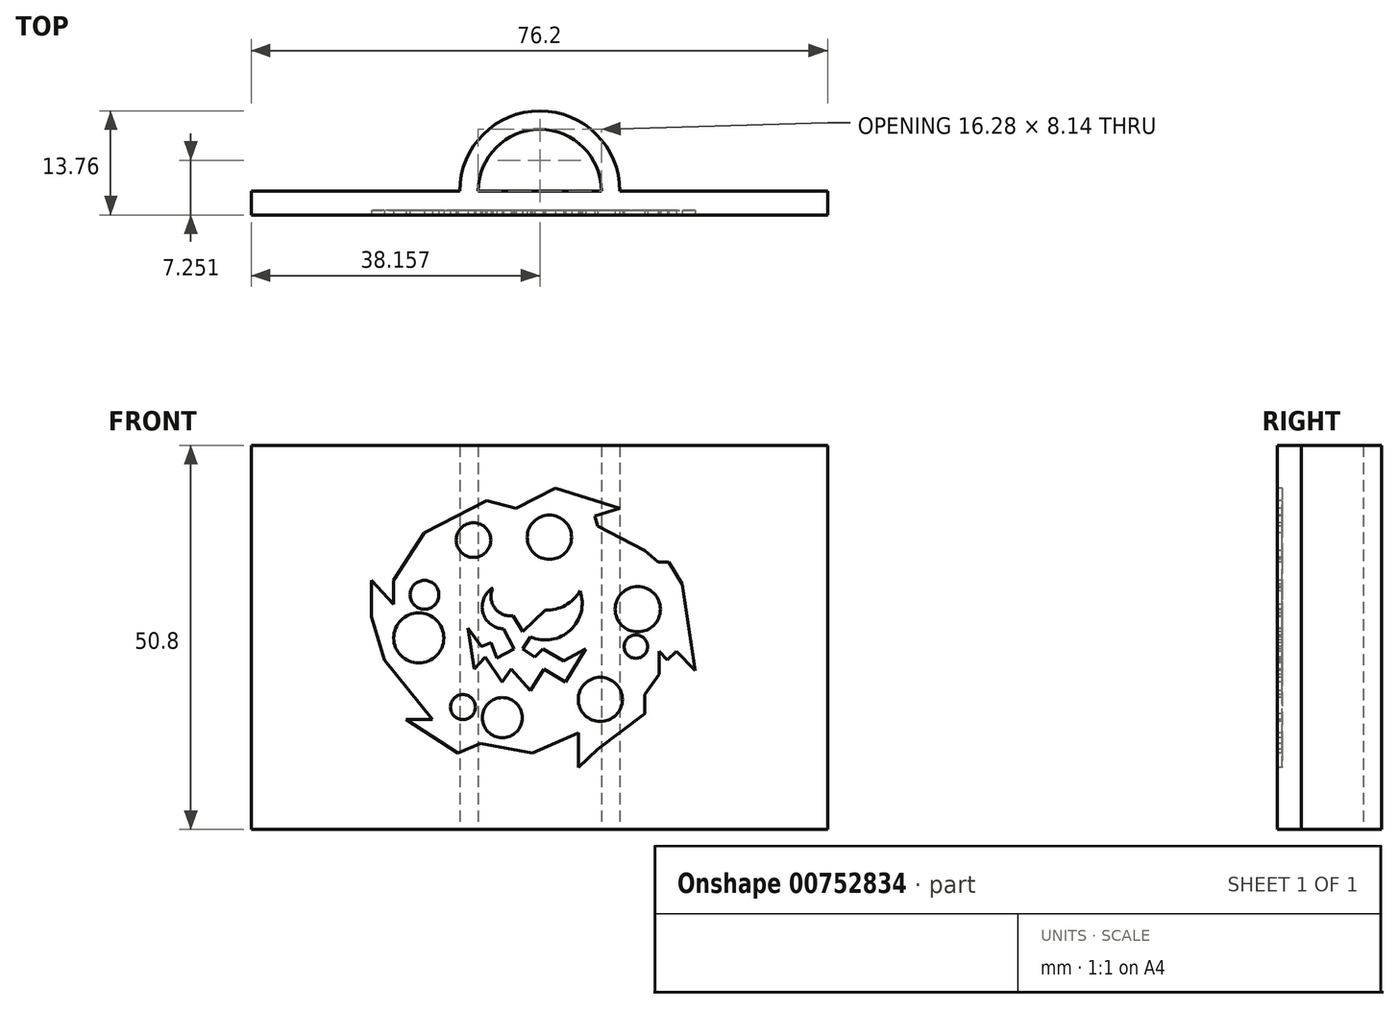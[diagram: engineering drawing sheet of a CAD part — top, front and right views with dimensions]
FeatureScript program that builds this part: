
annotation { "Feature Type Name" : "Feature", "Feature Type Description" : "" }
export const myFeature = defineFeature(function(context is Context, id is Id, definition is map)
    precondition{}
    {
        {
            var Q0;
            Q0=qCreatedBy(makeId("Front.planeOp"),FACE);
            var sketch = newSketch(context, id + "F0", { "sketchPlane" : qUnion([Q0])});
            skLineSegment(sketch, "E0.bottom", {"start": v(0, 0) * mm, "end": v(76.2, 0) * mm});
            skLineSegment(sketch, "E0.top", {"start": v(0, 50.8) * mm, "end": v(76.2, 50.8) * mm});
            skLineSegment(sketch, "E0.left", {"start": v(0, 0) * mm, "end": v(0, 50.8) * mm});
            skLineSegment(sketch, "E0.right", {"start": v(76.2, 0) * mm, "end": v(76.2, 50.8) * mm});
            skSolve(sketch);
        }
        {
            var Q0;
            Q0=makeQuery(id+"F0.imprint","IMPRINT",FACE,{"disambiguationData":[TD([[makeQuery(id+"F0.imprint","IMPRINT",EDGE,{"derivedFrom":sQuery(id+"F0.wireOp",EDGE,"E0.bottom")}),1.0]])]});
            extrude(context, id + "F1", {"entities" : qUnion([Q0]), "depth" : 3.17 * mm, "offsetDistance" : 25.4 * mm});
        }
        {
            var Q0;
            Q0=makeQuery(id+"F1.opExtrude","CAP_FACE",FACE,{"disambiguationData":[OSD([sQuery(id+"F0.wireOp",EDGE,"E0.bottom"),sQuery(id+"F0.wireOp",EDGE,"E0.top"),sQuery(id+"F0.wireOp",EDGE,"E0.left"),sQuery(id+"F0.wireOp",EDGE,"E0.right")])],"isStart":false});
            var sketch = newSketch(context, id + "F2", { "sketchPlane" : qUnion([Q0])});
            skLineSegment(sketch, "E1", {"start": v(40.18, 45.14) * mm, "end": v(48.7, 42.47) * mm});
            skLineSegment(sketch, "E2", {"start": v(48.7, 42.47) * mm, "end": v(45.39, 41.45) * mm});
            skLineSegment(sketch, "E3", {"start": v(45.39, 41.45) * mm, "end": v(45.8, 40.12) * mm});
            skLineSegment(sketch, "E4", {"start": v(45.8, 40.12) * mm, "end": v(52, 36.88) * mm});
            skLineSegment(sketch, "E5", {"start": v(52, 36.88) * mm, "end": v(53.77, 35.36) * mm});
            skLineSegment(sketch, "E6", {"start": v(53.77, 35.36) * mm, "end": v(55.17, 35.36) * mm});
            skLineSegment(sketch, "E7", {"start": v(55.17, 35.36) * mm, "end": v(56.95, 32.44) * mm});
            skLineSegment(sketch, "E8", {"start": v(56.95, 32.44) * mm, "end": v(58.66, 21) * mm});
            skLineSegment(sketch, "E9", {"start": v(58.66, 21) * mm, "end": v(56.18, 23.55) * mm});
            skLineSegment(sketch, "E10", {"start": v(56.18, 23.55) * mm, "end": v(55.03, 22.42) * mm});
            skLineSegment(sketch, "E11", {"start": v(55.03, 22.42) * mm, "end": v(53.93, 23.55) * mm});
            skLineSegment(sketch, "E12", {"start": v(53.93, 23.55) * mm, "end": v(53.93, 20.5) * mm});
            skLineSegment(sketch, "E13", {"start": v(53.93, 20.5) * mm, "end": v(52, 17.83) * mm});
            skLineSegment(sketch, "E14", {"start": v(52, 17.83) * mm, "end": v(52, 15.3) * mm});
            skLineSegment(sketch, "E15", {"start": v(52, 15.3) * mm, "end": v(45.8, 10.6) * mm});
            skLineSegment(sketch, "E16", {"start": v(45.8, 10.6) * mm, "end": v(43.23, 8.18) * mm});
            skLineSegment(sketch, "E17", {"start": v(43.23, 8.18) * mm, "end": v(43.23, 12.75) * mm});
            skLineSegment(sketch, "E18", {"start": v(43.23, 12.75) * mm, "end": v(37.13, 10.08) * mm});
            skLineSegment(sketch, "E19", {"start": v(37.13, 10.08) * mm, "end": v(30.28, 11.35) * mm});
            skLineSegment(sketch, "E20", {"start": v(30.28, 11.35) * mm, "end": v(27.36, 10.08) * mm});
            skLineSegment(sketch, "E21", {"start": v(27.36, 10.08) * mm, "end": v(20.5, 14.53) * mm});
            skLineSegment(sketch, "E22", {"start": v(20.5, 14.53) * mm, "end": v(23.93, 14.53) * mm});
            skLineSegment(sketch, "E23", {"start": v(23.93, 14.53) * mm, "end": v(17.58, 22.42) * mm});
            skLineSegment(sketch, "E24", {"start": v(17.58, 22.42) * mm, "end": v(15.86, 28.12) * mm});
            skLineSegment(sketch, "E25", {"start": v(15.86, 28.12) * mm, "end": v(15.86, 32.94) * mm});
            skLineSegment(sketch, "E26", {"start": v(15.86, 32.94) * mm, "end": v(18.84, 29.78) * mm});
            skLineSegment(sketch, "E27", {"start": v(18.84, 29.78) * mm, "end": v(18.84, 32.94) * mm});
            skLineSegment(sketch, "E28", {"start": v(18.84, 32.94) * mm, "end": v(22.9, 39.22) * mm});
            skLineSegment(sketch, "E29", {"start": v(22.9, 39.22) * mm, "end": v(31.17, 43.48) * mm});
            skLineSegment(sketch, "E30", {"start": v(31.17, 43.48) * mm, "end": v(34.98, 42.47) * mm});
            skLineSegment(sketch, "E31", {"start": v(34.98, 42.47) * mm, "end": v(40.18, 45.14) * mm});
            skCircle(sketch, "E32", {"center": v(39.42, 38.66) * mm, "radius": 2.93 * mm});
            skCircle(sketch, "E33", {"center": v(29.39, 38.28) * mm, "radius": 2.29 * mm});
            skCircle(sketch, "E34", {"center": v(22.91, 31.04) * mm, "radius": 1.9 * mm});
            skCircle(sketch, "E35", {"center": v(22.15, 25.32) * mm, "radius": 3.31 * mm});
            skCircle(sketch, "E36", {"center": v(28, 16.18) * mm, "radius": 1.66 * mm});
            skCircle(sketch, "E37", {"center": v(33.2, 14.78) * mm, "radius": 2.65 * mm});
            skCircle(sketch, "E38", {"center": v(46.15, 17.2) * mm, "radius": 2.92 * mm});
            skCircle(sketch, "E39", {"center": v(50.85, 24.18) * mm, "radius": 1.55 * mm});
            skCircle(sketch, "E40", {"center": v(51.1, 29.13) * mm, "radius": 2.99 * mm});
            skLineSegment(sketch, "E41", {"start": v(28.63, 26.6) * mm, "end": v(29.48, 21.23) * mm});
            skLineSegment(sketch, "E42", {"start": v(29.48, 21.23) * mm, "end": v(30.91, 22.78) * mm});
            skLineSegment(sketch, "E43", {"start": v(30.91, 22.78) * mm, "end": v(33.18, 19.49) * mm});
            skLineSegment(sketch, "E44", {"start": v(33.18, 19.49) * mm, "end": v(34.36, 21.23) * mm});
            skLineSegment(sketch, "E45", {"start": v(34.36, 21.23) * mm, "end": v(36.95, 18.37) * mm});
            skLineSegment(sketch, "E46", {"start": v(36.95, 18.37) * mm, "end": v(38.66, 21.23) * mm});
            skLineSegment(sketch, "E47", {"start": v(38.66, 21.23) * mm, "end": v(41.56, 19.49) * mm});
            skLineSegment(sketch, "E48", {"start": v(41.56, 19.49) * mm, "end": v(44.21, 23.9) * mm});
            skLineSegment(sketch, "E49", {"start": v(44.21, 23.9) * mm, "end": v(41.28, 22.28) * mm});
            skLineSegment(sketch, "E50", {"start": v(41.28, 22.28) * mm, "end": v(38.57, 23.9) * mm});
            skLineSegment(sketch, "E51", {"start": v(38.57, 23.9) * mm, "end": v(37.46, 22.78) * mm});
            skLineSegment(sketch, "E52", {"start": v(37.46, 22.78) * mm, "end": v(35.93, 23.9) * mm});
            skLineSegment(sketch, "E53", {"start": v(35.93, 23.9) * mm, "end": v(36.95, 25.47) * mm});
            skLineSegment(sketch, "E54", {"start": v(28.63, 26.6) * mm, "end": v(30.4, 24.18) * mm});
            skLineSegment(sketch, "E55", {"start": v(30.4, 24.18) * mm, "end": v(31.7, 24.69) * mm});
            skPoint(sketch, "E55.endSnap0", {"position": v(58.66, 24.69) * mm});
            skLineSegment(sketch, "E56", {"start": v(31.7, 24.69) * mm, "end": v(32.48, 22.7) * mm});
            skLineSegment(sketch, "E57", {"start": v(32.48, 22.7) * mm, "end": v(34.75, 23.9) * mm});
            skLineSegment(sketch, "E58", {"start": v(34.75, 23.9) * mm, "end": v(33.36, 26.53) * mm});
            skArc(sketch, "E59", {"start": v(31.93, 31.93) * mm, "mid": v(30.63, 28.7) * mm, "end": v(33.36, 26.53) * mm});
            skArc(sketch, "E60", {"start": v(31.93, 31.93) * mm, "mid": v(32.19, 29.3) * mm, "end": v(34.6, 28.24) * mm});
            skArc(sketch, "E61", {"start": v(36.95, 25.47) * mm, "mid": v(42.2, 26.37) * mm, "end": v(43.48, 31.55) * mm});
            skArc(sketch, "E62", {"start": v(38.89, 29) * mm, "mid": v(41.53, 29.65) * mm, "end": v(43.48, 31.55) * mm});
            skLineSegment(sketch, "E63", {"start": v(34.6, 28.24) * mm, "end": v(35.93, 26.17) * mm});
            skLineSegment(sketch, "E64", {"start": v(38.89, 29) * mm, "end": v(35.93, 26.17) * mm});
            skSolve(sketch);
        }
        {
            var Q0;
            Q0=makeQuery(id+"F2.imprint","IMPRINT",FACE,{"disambiguationData":[TD([[makeQuery(id+"F2.imprint","IMPRINT",EDGE,{"derivedFrom":sQuery(id+"F2.wireOp",EDGE,"E1")}),-1.0]])]});
            extrude(context, id + "F3", {"entities" : qUnion([Q0]), "operationType" : NewBodyOperationType.REMOVE, "oppositeDirection" : true, "depth" : 0.64 * mm, "offsetDistance" : 25.4 * mm});
        }
        {
            var Q0;
            Q0=qCreatedBy(makeId("Top.planeOp"),FACE);
            var sketch = newSketch(context, id + "F4", { "sketchPlane" : qUnion([Q0])});
            skArc(sketch, "E65", {"start": v(46.3, 0) * mm, "mid": v(38.16, 8.14) * mm, "end": v(30.02, 0) * mm});
            skArc(sketch, "E66", {"start": v(48.74, 0) * mm, "mid": v(38.16, 10.58) * mm, "end": v(27.58, 0) * mm});
            skLineSegment(sketch, "E67", {"start": v(27.58, 0) * mm, "end": v(30.02, 0) * mm});
            skLineSegment(sketch, "E68.trimOffspring", {"start": v(46.3, 0) * mm, "end": v(48.74, 0) * mm});
            skSolve(sketch);
        }
        {
            var Q0;
            Q0=makeQuery(id+"F4.imprint","IMPRINT",FACE,{"disambiguationData":[TD([[makeQuery(id+"F4.imprint","IMPRINT",EDGE,{"derivedFrom":sQuery(id+"F4.wireOp",EDGE,"Sh1y4hBJ-ikYm-zsdX-eVSe-7YIYH9IKeIr3")}),-1.0]])]});
            var Q1;
            Q1=makeQuery(id+"F4.imprint","IMPRINT",FACE,{"disambiguationData":[TD([[makeQuery(id+"F4.imprint","IMPRINT",EDGE,{"derivedFrom":sQuery(id+"F4.wireOp",EDGE,"E65")}),-1.0]])]});
            extrude(context, id + "F5", {"entities" : qUnion([Q0, Q1]), "operationType" : NewBodyOperationType.ADD, "depth" : 50.8 * mm, "offsetDistance" : 25.4 * mm});
        }
    });
